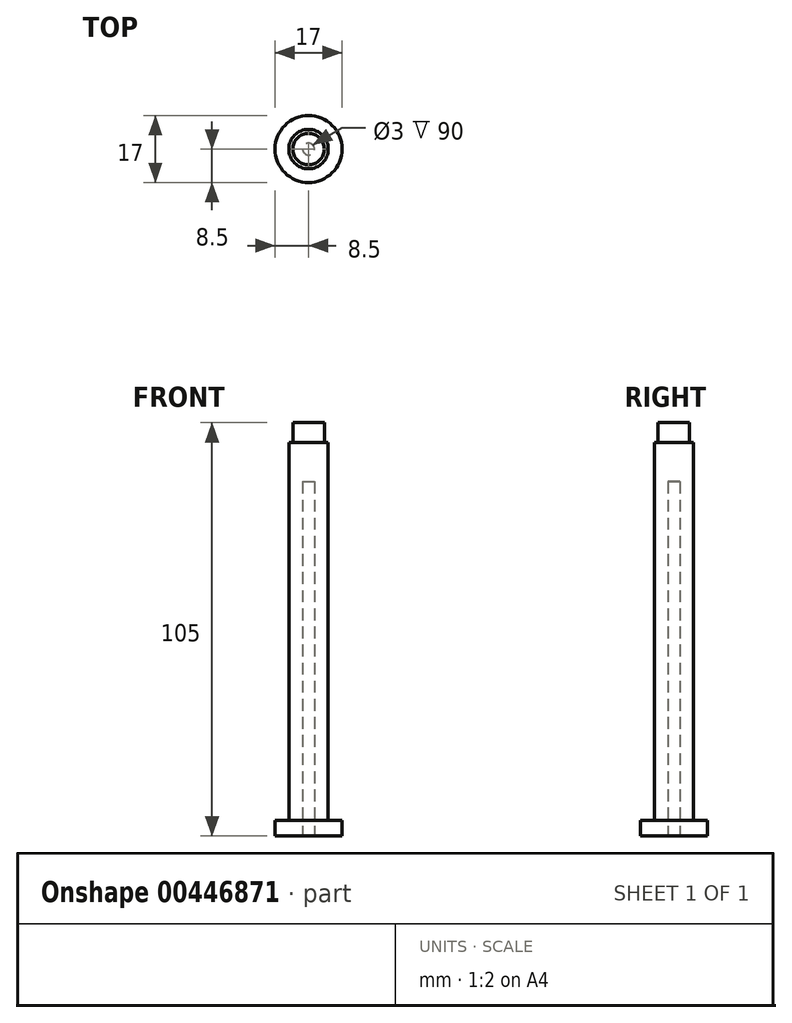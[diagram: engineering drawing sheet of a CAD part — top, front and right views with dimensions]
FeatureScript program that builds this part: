
annotation { "Feature Type Name" : "Feature", "Feature Type Description" : "" }
export const myFeature = defineFeature(function(context is Context, id is Id, definition is map)
    precondition{}
    {
        {
            var Q0;
            Q0=qCreatedBy(makeId("Top.planeOp"),FACE);
            var sketch = newSketch(context, id + "F0", { "sketchPlane" : qUnion([Q0])});
            skCircle(sketch, "E0", {"center": v(0, 0) * mm, "radius": 8.5 * mm});
            skSolve(sketch);
        }
        {
            var Q0;
            Q0=qSketchRegion(id+"F0",true);
            extrude(context, id + "F1", {"entities" : qUnion([Q0]), "depth" : 4 * mm});
        }
        {
            var Q0;
            Q0=qCreatedBy(makeId("Top.planeOp"),FACE);
            var sketch = newSketch(context, id + "F2", { "sketchPlane" : qUnion([Q0])});
            skCircle(sketch, "E1", {"center": v(0, 0) * mm, "radius": 5 * mm});
            skSolve(sketch);
        }
        {
            var Q0;
            Q0=qSketchRegion(id+"F2",true);
            extrude(context, id + "F3", {"entities" : qUnion([Q0]), "operationType" : NewBodyOperationType.ADD, "depth" : 100 * mm});
        }
        {
            var Q0;
            Q0=qCreatedBy(makeId("Right.planeOp"),FACE);
            var sketch = newSketch(context, id + "F4", { "sketchPlane" : qUnion([Q0])});
            skLineSegment(sketch, "E2.bottom", {"start": v(0, 105) * mm, "end": v(4, 105) * mm});
            skLineSegment(sketch, "E2.top", {"start": v(0, 100) * mm, "end": v(4, 100) * mm});
            skLineSegment(sketch, "E2.left", {"start": v(0, 105) * mm, "end": v(0, 100) * mm});
            skLineSegment(sketch, "E2.right", {"start": v(4, 105) * mm, "end": v(4, 100) * mm});
            skSolve(sketch);
        }
        {
            var Q0;
            Q0=makeQuery(id+"F4.imprint","IMPRINT",FACE,{"disambiguationData":[TD([[makeQuery(id+"F4.imprint","IMPRINT",EDGE,{"derivedFrom":sQuery(id+"F4.wireOp",EDGE,"E2.bottom")}),-1.0]])]});
            var Q1;
            Q1=sQuery(id+"F4.wireOp",EDGE,"E2.left");
            revolve(context, id + "F5", {"operationType" : NewBodyOperationType.ADD, "entities" : qUnion([Q0]), "axis" : qUnion([Q1]), "revolveType" : RevolveType.FULL});
        }
        {
            var Q0;
            Q0=makeQuery(id+"F1.opExtrude","CAP_FACE",FACE,{"disambiguationData":[OSD([sQuery(id+"F0.wireOp",EDGE,"E0")])],"isStart":true});
            var sketch = newSketch(context, id + "F6", { "sketchPlane" : qUnion([Q0])});
            skCircle(sketch, "E3", {"center": v(0, 0) * mm, "radius": 1.5 * mm});
            skSolve(sketch);
        }
        {
            var Q0;
            Q0=makeQuery(id+"F6.imprint","IMPRINT",FACE,{"disambiguationData":[TD([[makeQuery(id+"F6.imprint","IMPRINT",EDGE,{"derivedFrom":sQuery(id+"F6.wireOp",EDGE,"E3")}),1.0]])]});
            extrude(context, id + "F7", {"entities" : qUnion([Q0]), "operationType" : NewBodyOperationType.REMOVE, "oppositeDirection" : true, "depth" : 90 * mm});
        }
    });
